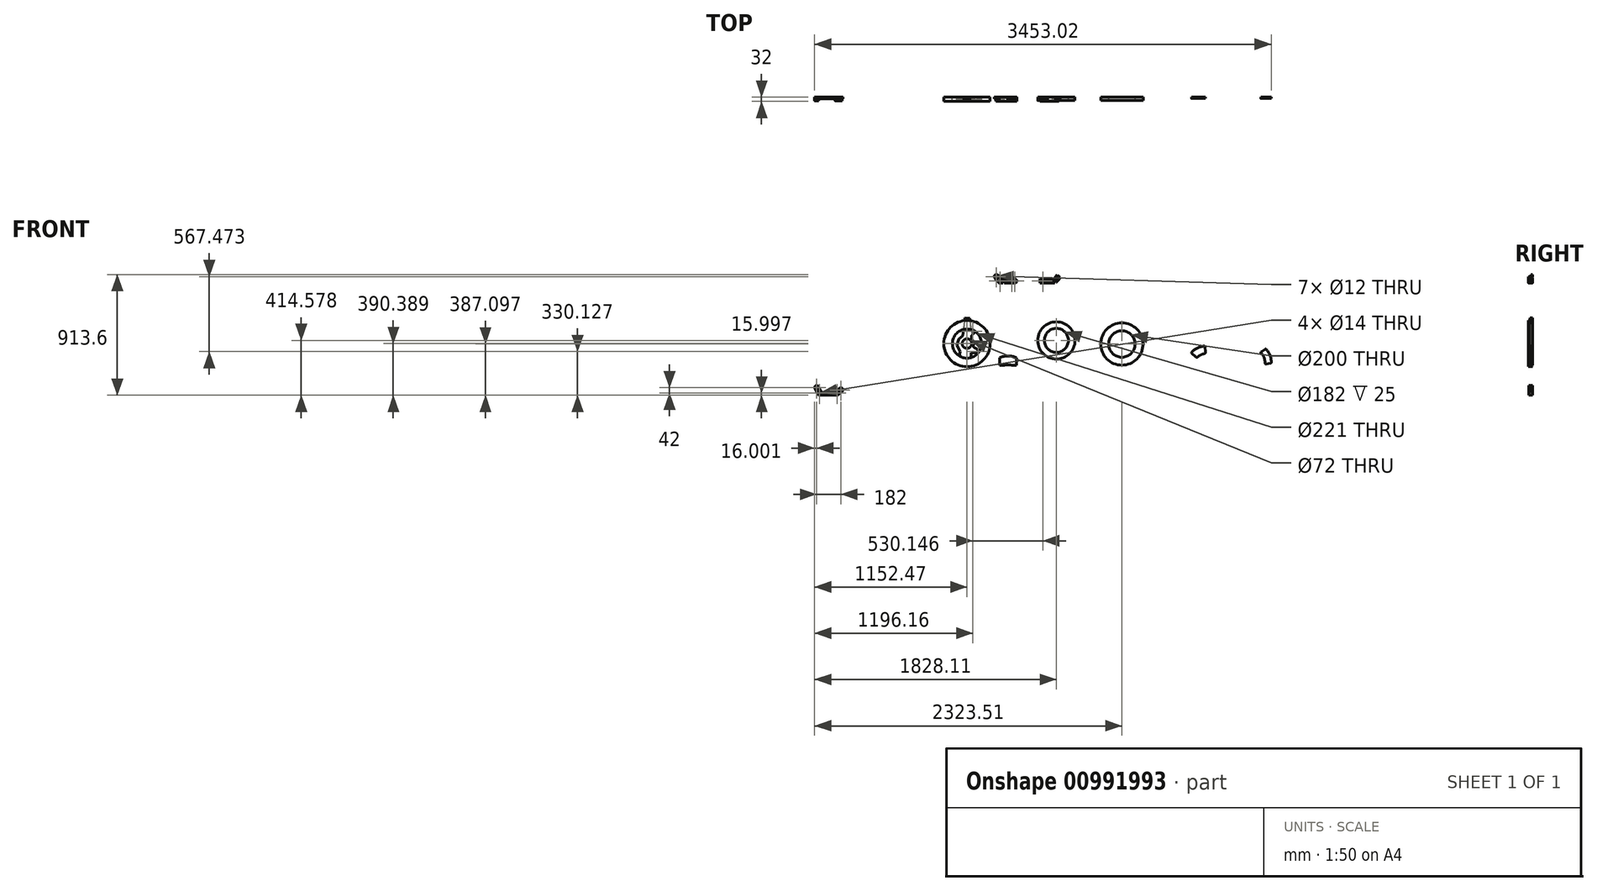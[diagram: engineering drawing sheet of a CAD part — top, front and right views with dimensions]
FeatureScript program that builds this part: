
annotation { "Feature Type Name" : "Feature", "Feature Type Description" : "" }
export const myFeature = defineFeature(function(context is Context, id is Id, definition is map)
    precondition{}
    {
        {
            var Q0;
            Q0=qCreatedBy(makeId("Front.planeOp"),FACE);
            var sketch = newSketch(context, id + "F0", { "sketchPlane" : qUnion([Q0])});
            skLineSegment(sketch, "E0", {"start": v(-162, 0) * mm, "end": v(162, 0) * mm, "construction": true});
            skCircle(sketch, "E1", {"center": v(0, 0) * mm, "radius": 162 * mm});
            skLineSegment(sketch, "E2", {"start": v(0, 162) * mm, "end": v(0, -162) * mm, "construction": true});
            skCircle(sketch, "E3", {"center": v(0, 0) * mm, "radius": 74.5 * mm, "construction": true});
            skLineSegment(sketch, "E4", {"start": v(0, 0) * mm, "end": v(76.6, 64.28) * mm, "construction": true});
            skLineSegment(sketch, "E5", {"start": v(0, 0) * mm, "end": v(77.96, -57.71) * mm, "construction": true});
            skLineSegment(sketch, "E6", {"start": v(76.6, 64.28) * mm, "end": v(77.96, -57.71) * mm, "construction": true});
            skCircle(sketch, "E7", {"center": v(76.6, 64.28) * mm, "radius": 6 * mm});
            skCircle(sketch, "E8", {"center": v(77.96, -57.71) * mm, "radius": 6 * mm});
            skArc(sketch, "E9", {"start": v(88.92, 55.71) * mm, "mid": v(89.19, 72.45) * mm, "end": v(73.8, 79.01) * mm});
            skArc(sketch, "E10", {"start": v(70.62, -70.8) * mm, "mid": v(91.06, -65.02) * mm, "end": v(85.23, -44.6) * mm});
            skLineSegment(sketch, "E11", {"start": v(35.43, -21.17) * mm, "end": v(88.92, 55.71) * mm});
            skLineSegment(sketch, "E12", {"start": v(37.52, -18.16) * mm, "end": v(85.23, -44.6) * mm});
            skArc(sketch, "E13.filletArc", {"start": v(59.66, 13.66) * mm, "mid": v(54.3, -14.26) * mm, "end": v(71.43, -36.95) * mm});
            skLineSegment(sketch, "E14", {"start": v(0, 0) * mm, "end": v(70.26, 84.63) * mm, "construction": true});
            skArc(sketch, "E15", {"start": v(65.94, 99) * mm, "mid": v(56.07, 89.49) * mm, "end": v(58.05, 75.92) * mm});
            skLineSegment(sketch, "E16", {"start": v(70.26, 84.63) * mm, "end": v(102.54, -22.62) * mm, "construction": true});
            skLineSegment(sketch, "E17", {"start": v(102.54, -22.62) * mm, "end": v(0, 0) * mm, "construction": true});
            skCircle(sketch, "E18", {"center": v(70.26, 84.63) * mm, "radius": 6 * mm});
            skCircle(sketch, "E19", {"center": v(102.54, -22.62) * mm, "radius": 6 * mm});
            skLineSegment(sketch, "E20", {"start": v(84.02, 39.53) * mm, "end": v(58.05, 75.92) * mm});
            skLineSegment(sketch, "E21", {"start": v(87.74, -25.06) * mm, "end": v(83.73, -30.58) * mm});
            skArc(sketch, "E22.filletArc", {"start": v(83.73, -30.58) * mm, "mid": v(95.18, 4.43) * mm, "end": v(84.02, 39.53) * mm});
            skArc(sketch, "E23.trimOffspring", {"start": v(87.74, -25.06) * mm, "mid": v(94.6, -35.35) * mm, "end": v(106.86, -36.98) * mm});
            skPoint(sketch, "E24.orphan", {"position": v(76.6, 79.28) * mm});
            skLineSegment(sketch, "E25", {"start": v(8.67, 66.58) * mm, "end": v(73.8, 79.01) * mm});
            skLineSegment(sketch, "E26", {"start": v(77.96, -57.71) * mm, "end": v(102.54, -22.62) * mm});
            skLineSegment(sketch, "E27", {"start": v(360.92, -8.62) * mm, "end": v(248.92, -8.62) * mm, "construction": true});
            skLineSegment(sketch, "E28", {"start": v(248.92, -8.62) * mm, "end": v(222.42, 24.88) * mm, "construction": true});
            skLineSegment(sketch, "E29", {"start": v(222.42, 24.88) * mm, "end": v(386.22, 24.88) * mm, "construction": true});
            skLineSegment(sketch, "E30", {"start": v(222.42, 24.88) * mm, "end": v(222.42, -34.6) * mm, "construction": true});
            skCircle(sketch, "E31", {"center": v(222.42, 24.88) * mm, "radius": 6 * mm});
            skCircle(sketch, "E32", {"center": v(248.92, -8.62) * mm, "radius": 6 * mm});
            skCircle(sketch, "E33", {"center": v(360.92, -8.62) * mm, "radius": 6 * mm});
            skCircle(sketch, "E34", {"center": v(339.42, -8.62) * mm, "radius": 6 * mm});
            skCircle(sketch, "E35", {"center": v(222.42, 24.88) * mm, "radius": 16 * mm});
            skCircle(sketch, "E36", {"center": v(248.92, -8.62) * mm, "radius": 16 * mm});
            skCircle(sketch, "E37", {"center": v(360.92, -8.62) * mm, "radius": 16 * mm});
            skCircle(sketch, "E38", {"center": v(339.42, -8.62) * mm, "radius": 15 * mm});
            skLineSegment(sketch, "E39", {"start": v(248.92, -24.62) * mm, "end": v(360.92, -24.62) * mm});
            skLineSegment(sketch, "E40", {"start": v(360.92, -24.62) * mm, "end": v(360.92, 7.38) * mm});
            skLineSegment(sketch, "E41", {"start": v(360.92, 7.38) * mm, "end": v(266.34, 7.38) * mm});
            skPoint(sketch, "E42.newPointA", {"position": v(248.92, 7.38) * mm});
            skLineSegment(sketch, "E43", {"start": v(37.52, -18.16) * mm, "end": v(77.52, -17.72) * mm});
            skLineSegment(sketch, "E44.trimOffspring", {"start": v(305.92, 7.38) * mm, "end": v(327.67, -17.95) * mm});
            skLineSegment(sketch, "E45", {"start": v(357.92, 7.38) * mm, "end": v(354.13, -11.56) * mm});
            skLineSegment(sketch, "E46.0", {"start": v(236.37, -18.55) * mm, "end": v(209.87, 14.95) * mm});
            skLineSegment(sketch, "E47.0", {"start": v(250.66, 14.97) * mm, "end": v(234.97, 34.8) * mm});
            skLineSegment(sketch, "E48.0", {"start": v(219.55, 2.71) * mm, "end": v(245.14, 21.95) * mm});
            skLineSegment(sketch, "E49", {"start": v(456.63, 91.81) * mm, "end": v(456.63, -58.74) * mm});
            skLineSegment(sketch, "E50.MirrorCS", {"start": v(555.34, 7.38) * mm, "end": v(559.13, -11.56) * mm});
            skLineSegment(sketch, "E51.MirrorCS", {"start": v(664.34, -8.62) * mm, "end": v(690.84, 24.88) * mm, "construction": true});
            skCircle(sketch, "E52.MirrorC", {"center": v(664.34, -8.62) * mm, "radius": 6 * mm});
            skLineSegment(sketch, "E53.MirrorCS", {"start": v(676.89, -18.55) * mm, "end": v(703.39, 14.95) * mm});
            skCircle(sketch, "E54.MirrorC", {"center": v(690.84, 24.88) * mm, "radius": 6 * mm});
            skCircle(sketch, "E55.MirrorC", {"center": v(552.34, -8.62) * mm, "radius": 16 * mm});
            skLineSegment(sketch, "E56.MirrorCS", {"start": v(552.34, 7.38) * mm, "end": v(646.91, 7.38) * mm});
            skCircle(sketch, "E57.MirrorC", {"center": v(664.34, -8.62) * mm, "radius": 16 * mm});
            skLineSegment(sketch, "E58.MirrorCS", {"start": v(607.34, 7.38) * mm, "end": v(585.59, -17.95) * mm});
            skLineSegment(sketch, "E59.MirrorCS", {"start": v(693.7, 2.71) * mm, "end": v(668.12, 21.95) * mm});
            skCircle(sketch, "E60.MirrorC", {"center": v(552.34, -8.62) * mm, "radius": 6 * mm});
            skLineSegment(sketch, "E61.MirrorCS", {"start": v(552.34, -24.62) * mm, "end": v(552.34, 7.38) * mm});
            skLineSegment(sketch, "E62.MirrorCS", {"start": v(552.34, -8.62) * mm, "end": v(664.34, -8.62) * mm, "construction": true});
            skPoint(sketch, "E63.MirrorP", {"position": v(664.34, 7.38) * mm});
            skLineSegment(sketch, "E64.MirrorCS", {"start": v(690.84, 24.88) * mm, "end": v(527.04, 24.88) * mm, "construction": true});
            skLineSegment(sketch, "E65.MirrorCS", {"start": v(690.84, 24.88) * mm, "end": v(690.84, -34.6) * mm, "construction": true});
            skLineSegment(sketch, "E66.MirrorCS", {"start": v(664.34, -24.62) * mm, "end": v(552.34, -24.62) * mm});
            skCircle(sketch, "E67.MirrorC", {"center": v(690.84, 24.88) * mm, "radius": 16 * mm});
            skCircle(sketch, "E68.MirrorC", {"center": v(573.84, -8.62) * mm, "radius": 15 * mm});
            skCircle(sketch, "E69.MirrorC", {"center": v(573.84, -8.62) * mm, "radius": 6 * mm});
            skLineSegment(sketch, "E70.MirrorCS", {"start": v(662.6, 14.97) * mm, "end": v(678.29, 34.8) * mm});
            skPoint(sketch, "E71.visualSharp", {"position": v(256.66, 7.38) * mm});
            skArc(sketch, "E71.filletArc", {"start": v(250.66, 14.97) * mm, "mid": v(257.63, 9.38) * mm, "end": v(266.34, 7.38) * mm});
            skPoint(sketch, "E72.visualSharp", {"position": v(656.6, 7.38) * mm});
            skArc(sketch, "E72.filletArc", {"start": v(646.91, 7.38) * mm, "mid": v(655.63, 9.38) * mm, "end": v(662.6, 14.97) * mm});
            skLineSegment(sketch, "E73", {"start": v(360.92, -14.62) * mm, "end": v(248.92, -14.62) * mm, "construction": true});
            skLineSegment(sketch, "E74", {"start": v(354.92, -8.62) * mm, "end": v(354.92, -24.62) * mm, "construction": true});
            skLineSegment(sketch, "E75.0", {"start": v(338.92, -15.62) * mm, "end": v(338.92, -24.62) * mm, "construction": true});
            skCircle(sketch, "E76", {"center": v(360.92, -8.62) * mm, "radius": 18 * mm, "construction": true});
            skLineSegment(sketch, "E77.0", {"start": v(333.92, -10.62) * mm, "end": v(333.92, -10.62) * mm});
            skLineSegment(sketch, "E78.0", {"start": v(328.92, -15.62) * mm, "end": v(328.92, -24.62) * mm, "construction": true});
            skArc(sketch, "E79.filletArc", {"start": v(333.92, -10.62) * mm, "mid": v(330.38, -12.09) * mm, "end": v(328.92, -15.62) * mm, "construction": true});
            skArc(sketch, "E80.filletArc", {"start": v(338.92, -15.62) * mm, "mid": v(337.45, -12.09) * mm, "end": v(333.92, -10.62) * mm, "construction": true});
            skLineSegment(sketch, "E81.0", {"start": v(280.92, -15.62) * mm, "end": v(280.92, -24.62) * mm});
            skLineSegment(sketch, "E82.0", {"start": v(270.92, -15.62) * mm, "end": v(270.92, -24.62) * mm});
            skArc(sketch, "E83", {"start": v(280.92, -15.62) * mm, "mid": v(275.92, -10.62) * mm, "end": v(270.92, -15.62) * mm});
            skSolve(sketch);
        }
        {
            var Q0;
            Q0=makeQuery(id+"F0.imprint","IMPRINT",FACE,{"disambiguationData":[TD([[makeQuery(id+"F0.imprint","IMPRINT",EDGE,{"derivedFrom":sQuery(id+"F0.wireOp",EDGE,"E31")}),-1.0]])]});
            var Q1;
            {var subQ0=sQuery(id+"F0.wireOp",EDGE,"E47.0");var subQ1=sQuery(id+"F0.wireOp",EDGE,"E35");var subQ2=makeQuery(id+"F0.imprint","INTERSECT",VERTEX,{"derivedFrom":[subQ1,subQ0]});Q1=makeQuery(id+"F0.imprint","IMPRINT",FACE,{"disambiguationData":[TD([[makeQuery(id+"F0.imprint","IMPRINT",EDGE,{"disambiguationData":[TD([[subQ2,1.0]])],"derivedFrom":subQ1}),-1.0]])]});}
            var Q2;
            {var subQ0=sQuery(id+"F0.wireOp",EDGE,"E46.0");var subQ1=sQuery(id+"F0.wireOp",EDGE,"E35");var subQ2=makeQuery(id+"F0.imprint","INTERSECT",VERTEX,{"derivedFrom":[subQ1,subQ0]});Q2=makeQuery(id+"F0.imprint","IMPRINT",FACE,{"disambiguationData":[TD([[makeQuery(id+"F0.imprint","IMPRINT",EDGE,{"disambiguationData":[TD([[subQ2,-1.0]])],"derivedFrom":subQ1}),-1.0]])]});}
            var Q3;
            {var subQ0=sQuery(id+"F0.wireOp",EDGE,"E45");var subQ1=sQuery(id+"F0.wireOp",EDGE,"E37");var subQ2=makeQuery(id+"F0.imprint","INTERSECT",VERTEX,{"derivedFrom":[subQ1,subQ0]});Q3=makeQuery(id+"F0.imprint","IMPRINT",FACE,{"disambiguationData":[TD([[makeQuery(id+"F0.imprint","IMPRINT",EDGE,{"disambiguationData":[TD([[subQ2,-1.0]])],"derivedFrom":subQ1}),1.0]])]});}
            var Q4;
            {var subQ0=sQuery(id+"F0.wireOp",EDGE,"E44.trimOffspring");Q4=makeQuery(id+"F0.imprint","IMPRINT",FACE,{"disambiguationData":[TD([[makeQuery(id+"F0.imprint","IMPRINT",EDGE,{"derivedFrom":subQ0}),1.0]])]});}
            var Q5;
            {var subQ2=sQuery(id+"F0.wireOp",EDGE,"E37");var subQ4=sQuery(id+"F0.wireOp",EDGE,"E34");var subQ6=makeQuery(id+"F0.imprint","INTERSECT",VERTEX,{"disambiguationData":[OD(0.0)],"derivedFrom":[subQ4,subQ2]});Q5=makeQuery(id+"F0.imprint","IMPRINT",FACE,{"disambiguationData":[TD([[makeQuery(id+"F0.imprint","IMPRINT",EDGE,{"disambiguationData":[TD([[subQ6,1.0]])],"derivedFrom":subQ4}),-1.0]])]});}
            var Q6;
            {var subQ0=sQuery(id+"F0.wireOp",EDGE,"E37");var subQ1=sQuery(id+"F0.wireOp",EDGE,"E34");var subQ7=makeQuery(id+"F0.imprint","INTERSECT",VERTEX,{"disambiguationData":[OD(0.0)],"derivedFrom":[subQ1,subQ0]});Q6=makeQuery(id+"F0.imprint","IMPRINT",FACE,{"disambiguationData":[TD([[makeQuery(id+"F0.imprint","IMPRINT",EDGE,{"disambiguationData":[TD([[subQ7,-1.0]])],"derivedFrom":subQ1}),-1.0]])]});}
            extrude(context, id + "F1", {"entities" : qUnion([Q0, Q1, Q2, Q3, Q4, Q5, Q6]), "depth" : 12 * mm, "offsetDistance" : 25 * mm});
        }
        {
            var Q0;
            {var subQ0=sQuery(id+"F0.wireOp",EDGE,"E40");var subQ1=sQuery(id+"F0.wireOp",EDGE,"E33");var subQ2=makeQuery(id+"F0.imprint","INTERSECT",VERTEX,{"disambiguationData":[OD(0.0)],"derivedFrom":[subQ1,subQ0]});Q0=makeQuery(id+"F0.imprint","IMPRINT",FACE,{"disambiguationData":[TD([[makeQuery(id+"F0.imprint","IMPRINT",EDGE,{"disambiguationData":[TD([[subQ2,-1.0]])],"derivedFrom":subQ1}),-1.0]])]});}
            var Q1;
            {var subQ5=sQuery(id+"F0.wireOp",EDGE,"E40");var subQ9=sQuery(id+"F0.wireOp",EDGE,"E33");var subQ10=makeQuery(id+"F0.imprint","INTERSECT",VERTEX,{"disambiguationData":[OD(0.0)],"derivedFrom":[subQ9,subQ5]});Q1=makeQuery(id+"F0.imprint","IMPRINT",FACE,{"disambiguationData":[TD([[makeQuery(id+"F0.imprint","IMPRINT",EDGE,{"disambiguationData":[TD([[subQ10,1.0]])],"derivedFrom":subQ9}),-1.0]])]});}
            var Q2;
            {var subQ0=sQuery(id+"F0.wireOp",EDGE,"E41");var subQ3=sQuery(id+"F0.wireOp",EDGE,"E45");var subQ5=makeQuery(id+"F0.imprint","INTERSECT",VERTEX,{"derivedFrom":[subQ0,subQ3]});Q2=makeQuery(id+"F0.imprint","IMPRINT",FACE,{"disambiguationData":[TD([[makeQuery(id+"F0.imprint","IMPRINT",EDGE,{"disambiguationData":[TD([[subQ5,-1.0]])],"derivedFrom":subQ3}),1.0]])]});}
            var Q3;
            {var subQ12=sQuery(id+"F0.wireOp",EDGE,"E39");Q3=makeQuery(id+"F0.imprint","IMPRINT",FACE,{"disambiguationData":[TD([[makeQuery(id+"F0.imprint","IMPRINT",EDGE,{"derivedFrom":subQ12}),1.0]])]});}
            var Q4;
            Q4=makeQuery(id+"F0.imprint","IMPRINT",FACE,{"disambiguationData":[TD([[makeQuery(id+"F0.imprint","IMPRINT",EDGE,{"derivedFrom":sQuery(id+"F0.wireOp",EDGE,"E32")}),-1.0]])]});
            extrude(context, id + "F2", {"entities" : qUnion([Q0, Q1, Q2, Q3, Q4]), "depth" : 30 * mm, "offsetDistance" : 25 * mm});
        }
        {
            var Q0;
            {var subQ0=sQuery(id+"F0.wireOp",EDGE,"E58.MirrorCS");Q0=makeQuery(id+"F0.imprint","IMPRINT",FACE,{"disambiguationData":[TD([[makeQuery(id+"F0.imprint","IMPRINT",EDGE,{"derivedFrom":subQ0}),-1.0]])]});}
            var Q1;
            {var subQ0=sQuery(id+"F0.wireOp",EDGE,"E68.MirrorC");var subQ2=sQuery(id+"F0.wireOp",EDGE,"E55.MirrorC");var subQ3=makeQuery(id+"F0.imprint","INTERSECT",VERTEX,{"disambiguationData":[OD(0.0)],"derivedFrom":[subQ2,subQ0]});Q1=makeQuery(id+"F0.imprint","IMPRINT",FACE,{"disambiguationData":[TD([[makeQuery(id+"F0.imprint","IMPRINT",EDGE,{"disambiguationData":[TD([[subQ3,-1.0]])],"derivedFrom":subQ2}),1.0]])]});}
            var Q2;
            {var subQ0=sQuery(id+"F0.wireOp",EDGE,"E68.MirrorC");var subQ2=sQuery(id+"F0.wireOp",EDGE,"E55.MirrorC");var subQ4=makeQuery(id+"F0.imprint","INTERSECT",VERTEX,{"disambiguationData":[OD(0.0)],"derivedFrom":[subQ2,subQ0]});Q2=makeQuery(id+"F0.imprint","IMPRINT",FACE,{"disambiguationData":[TD([[makeQuery(id+"F0.imprint","IMPRINT",EDGE,{"disambiguationData":[TD([[subQ4,-1.0]])],"derivedFrom":subQ2}),-1.0]])]});}
            var Q3;
            {var subQ0=sQuery(id+"F0.wireOp",EDGE,"E68.MirrorC");var subQ1=sQuery(id+"F0.wireOp",EDGE,"E50.MirrorCS");var subQ2=makeQuery(id+"F0.imprint","INTERSECT",VERTEX,{"derivedFrom":[subQ1,subQ0]});Q3=makeQuery(id+"F0.imprint","IMPRINT",FACE,{"disambiguationData":[TD([[makeQuery(id+"F0.imprint","IMPRINT",EDGE,{"disambiguationData":[TD([[subQ2,1.0]])],"derivedFrom":subQ1}),1.0]])]});}
            var Q4;
            Q4=makeQuery(id+"F0.imprint","IMPRINT",FACE,{"disambiguationData":[TD([[makeQuery(id+"F0.imprint","IMPRINT",EDGE,{"derivedFrom":sQuery(id+"F0.wireOp",EDGE,"E54.MirrorC")}),1.0]])]});
            var Q5;
            {var subQ0=sQuery(id+"F0.wireOp",EDGE,"E70.MirrorCS");var subQ1=sQuery(id+"F0.wireOp",EDGE,"E59.MirrorCS");var subQ2=makeQuery(id+"F0.imprint","INTERSECT",VERTEX,{"derivedFrom":[subQ1,subQ0]});Q5=makeQuery(id+"F0.imprint","IMPRINT",FACE,{"disambiguationData":[TD([[makeQuery(id+"F0.imprint","IMPRINT",EDGE,{"disambiguationData":[TD([[subQ2,1.0]])],"derivedFrom":subQ1}),-1.0]])]});}
            var Q6;
            {var subQ0=sQuery(id+"F0.wireOp",EDGE,"E67.MirrorC");var subQ1=sQuery(id+"F0.wireOp",EDGE,"E53.MirrorCS");var subQ2=makeQuery(id+"F0.imprint","INTERSECT",VERTEX,{"derivedFrom":[subQ1,subQ0]});Q6=makeQuery(id+"F0.imprint","IMPRINT",FACE,{"disambiguationData":[TD([[makeQuery(id+"F0.imprint","IMPRINT",EDGE,{"disambiguationData":[TD([[subQ2,1.0]])],"derivedFrom":subQ1}),1.0]])]});}
            extrude(context, id + "F3", {"entities" : qUnion([Q0, Q1, Q2, Q3, Q4, Q5, Q6]), "depth" : 12 * mm, "offsetDistance" : 25 * mm});
        }
        {
            var Q0;
            {var subQ0=sQuery(id+"F0.wireOp",EDGE,"E61.MirrorCS");var subQ4=sQuery(id+"F0.wireOp",EDGE,"E60.MirrorC");var subQ5=makeQuery(id+"F0.imprint","INTERSECT",VERTEX,{"disambiguationData":[OD(0.0)],"derivedFrom":[subQ4,subQ0]});Q0=makeQuery(id+"F0.imprint","IMPRINT",FACE,{"disambiguationData":[TD([[makeQuery(id+"F0.imprint","IMPRINT",EDGE,{"disambiguationData":[TD([[subQ5,-1.0]])],"derivedFrom":subQ4}),1.0]])]});}
            var Q1;
            {var subQ6=sQuery(id+"F0.wireOp",EDGE,"E68.MirrorC");var subQ9=sQuery(id+"F0.wireOp",EDGE,"E50.MirrorCS");var subQ11=makeQuery(id+"F0.imprint","INTERSECT",VERTEX,{"derivedFrom":[subQ9,subQ6]});Q1=makeQuery(id+"F0.imprint","IMPRINT",FACE,{"disambiguationData":[TD([[makeQuery(id+"F0.imprint","IMPRINT",EDGE,{"disambiguationData":[TD([[subQ11,1.0]])],"derivedFrom":subQ9}),-1.0]])]});}
            var Q2;
            {var subQ0=sQuery(id+"F0.wireOp",EDGE,"E56.MirrorCS");var subQ1=sQuery(id+"F0.wireOp",EDGE,"E50.MirrorCS");var subQ2=makeQuery(id+"F0.imprint","INTERSECT",VERTEX,{"derivedFrom":[subQ1,subQ0]});Q2=makeQuery(id+"F0.imprint","IMPRINT",FACE,{"disambiguationData":[TD([[makeQuery(id+"F0.imprint","IMPRINT",EDGE,{"disambiguationData":[TD([[subQ2,-1.0]])],"derivedFrom":subQ1}),-1.0]])]});}
            var Q3;
            {var subQ9=sQuery(id+"F0.wireOp",EDGE,"E58.MirrorCS");Q3=makeQuery(id+"F0.imprint","IMPRINT",FACE,{"disambiguationData":[TD([[makeQuery(id+"F0.imprint","IMPRINT",EDGE,{"derivedFrom":subQ9}),1.0]])]});}
            var Q4;
            Q4=makeQuery(id+"F0.imprint","IMPRINT",FACE,{"disambiguationData":[TD([[makeQuery(id+"F0.imprint","IMPRINT",EDGE,{"derivedFrom":sQuery(id+"F0.wireOp",EDGE,"E52.MirrorC")}),1.0]])]});
            extrude(context, id + "F4", {"entities" : qUnion([Q0, Q1, Q2, Q3, Q4]), "depth" : 30 * mm, "offsetDistance" : 25 * mm});
        }
        {
            var Q0;
            Q0=qCreatedBy(makeId("Front.planeOp"),FACE);
            var sketch = newSketch(context, id + "F5", { "sketchPlane" : qUnion([Q0])});
            skLineSegment(sketch, "E84", {"start": v(0, -307.33) * mm, "end": v(0, -657.33) * mm, "construction": true});
            skLineSegment(sketch, "E85", {"start": v(-175, -482.33) * mm, "end": v(175, -482.33) * mm, "construction": true});
            skCircle(sketch, "E86", {"center": v(0, -482.33) * mm, "radius": 36 * mm});
            skCircle(sketch, "E87", {"center": v(0, -482.33) * mm, "radius": 57.15 * mm, "construction": true});
            skCircle(sketch, "E88", {"center": v(0, -482.33) * mm, "radius": 175 * mm});
            skCircle(sketch, "E89", {"center": v(57.15, -482.33) * mm, "radius": 6.1 * mm});
            skCircle(sketch, "E90.1.0", {"center": v(17.66, -536.68) * mm, "radius": 6.1 * mm});
            skCircle(sketch, "E90.2.0", {"center": v(-46.24, -515.92) * mm, "radius": 6.1 * mm});
            skCircle(sketch, "E90.3.0", {"center": v(-46.24, -448.74) * mm, "radius": 6.1 * mm});
            skCircle(sketch, "E90.4.0", {"center": v(17.66, -427.98) * mm, "radius": 6.1 * mm});
            skCircle(sketch, "E91", {"center": v(43.7, -387.95) * mm, "radius": 6 * mm});
            skCircle(sketch, "E92", {"center": v(84.76, -542.6) * mm, "radius": 6 * mm});
            skArc(sketch, "E93", {"start": v(48.18, -495.7) * mm, "mid": v(48.92, -471.99) * mm, "end": v(38.64, -450.6) * mm});
            skArc(sketch, "E94", {"start": v(84.07, -554.44) * mm, "mid": v(96.16, -545.89) * mm, "end": v(90.49, -532.2) * mm});
            skArc(sketch, "E95", {"start": v(54.93, -397.9) * mm, "mid": v(57.08, -381.18) * mm, "end": v(42.33, -373.02) * mm});
            skLineSegment(sketch, "E96", {"start": v(55.4, -512.86) * mm, "end": v(90.49, -532.2) * mm});
            skArc(sketch, "E97.filletArc", {"start": v(48.18, -495.7) * mm, "mid": v(48.8, -505.54) * mm, "end": v(55.4, -512.86) * mm});
            skLineSegment(sketch, "E98", {"start": v(39.29, -415.57) * mm, "end": v(54.93, -397.9) * mm});
            skPoint(sketch, "E99.visualSharp", {"position": v(20.54, -436.75) * mm});
            skArc(sketch, "E99.filletArc", {"start": v(39.29, -415.57) * mm, "mid": v(32.5, -432.96) * mm, "end": v(38.64, -450.6) * mm});
            skLineSegment(sketch, "E100", {"start": v(21.57, -550.77) * mm, "end": v(84.07, -554.44) * mm});
            skLineSegment(sketch, "E101", {"start": v(10.62, -375.9) * mm, "end": v(42.33, -373.02) * mm});
            skCircle(sketch, "E102", {"center": v(0, -482.33) * mm, "radius": 110.5 * mm});
            skLineSegment(sketch, "E103.0", {"start": v(246.52, -647.5) * mm, "end": v(277.02, -647.5) * mm});
            skLineSegment(sketch, "E104", {"start": v(246.52, -647.5) * mm, "end": v(246.52, -588.5) * mm});
            skLineSegment(sketch, "E105.0", {"start": v(374.52, -647.5) * mm, "end": v(374.52, -588.5) * mm});
            skArc(sketch, "E106", {"start": v(374.52, -588.5) * mm, "mid": v(310.52, -576.5) * mm, "end": v(246.52, -588.5) * mm});
            skArc(sketch, "E107", {"start": v(344.02, -647.5) * mm, "mid": v(310.52, -642.32) * mm, "end": v(277.02, -647.5) * mm});
            skLineSegment(sketch, "E108.trimOffspring", {"start": v(344.02, -647.5) * mm, "end": v(374.52, -647.5) * mm});
            skLineSegment(sketch, "E109", {"start": v(20.52, -289.6) * mm, "end": v(27.5, -374.37) * mm});
            skLineSegment(sketch, "E110", {"start": v(-17.97, -286.17) * mm, "end": v(-32.55, -424.34) * mm});
            skLineSegment(sketch, "E111", {"start": v(-32.55, -424.34) * mm, "end": v(-59.93, -445.81) * mm});
            skLineSegment(sketch, "E112", {"start": v(-59.93, -445.81) * mm, "end": v(-76.28, -493.3) * mm});
            skLineSegment(sketch, "E113", {"start": v(-76.28, -493.3) * mm, "end": v(-52.2, -540.3) * mm});
            skLineSegment(sketch, "E114", {"start": v(-52.2, -540.3) * mm, "end": v(-58.88, -590.81) * mm});
            skLineSegment(sketch, "E115", {"start": v(-58.88, -590.81) * mm, "end": v(28.35, -593.9) * mm});
            skLineSegment(sketch, "E116", {"start": v(20.52, -289.6) * mm, "end": v(-17.97, -286.17) * mm});
            skCircle(sketch, "E117", {"center": v(0, -482.33) * mm, "radius": 104 * mm, "construction": true});
            skCircle(sketch, "E118", {"center": v(75.37, -545.98) * mm, "radius": 7 * mm, "construction": true});
            skCircle(sketch, "E119", {"center": v(36.66, -390.74) * mm, "radius": 7 * mm, "construction": true});
            skCircle(sketch, "E120", {"center": v(0, -482.33) * mm, "radius": 98.65 * mm, "construction": true});
            skArc(sketch, "E121", {"start": v(39.16, -556.6) * mm, "mid": v(87.53, -496.9) * mm, "end": v(60.86, -424.84) * mm, "construction": true});
            skLineSegment(sketch, "E122.0", {"start": v(30.14, -551.27) * mm, "end": v(30.14, -603.24) * mm});
            skCircle(sketch, "E123", {"center": v(43.08, -571.08) * mm, "radius": 7 * mm, "construction": true});
            skCircle(sketch, "E124", {"center": v(70.65, -413.47) * mm, "radius": 7 * mm, "construction": true});
            skLineSegment(sketch, "E125", {"start": v(70.65, -413.47) * mm, "end": v(43.08, -571.08) * mm, "construction": true});
            skCircle(sketch, "E126", {"center": v(70.65, -413.47) * mm, "radius": 15 * mm, "construction": true});
            skCircle(sketch, "E127", {"center": v(43.08, -571.08) * mm, "radius": 15 * mm, "construction": true});
            skLineSegment(sketch, "E128", {"start": v(56.87, -492.28) * mm, "end": v(87.4, -497.62) * mm, "construction": true});
            skArc(sketch, "E129.0", {"start": v(100.46, -540.33) * mm, "mid": v(114.99, -502.42) * mm, "end": v(114.14, -461.83) * mm, "construction": true});
            skLineSegment(sketch, "E130", {"start": v(43.08, -571.08) * mm, "end": v(100.46, -540.33) * mm, "construction": true});
            skLineSegment(sketch, "E131", {"start": v(70.65, -413.47) * mm, "end": v(114.14, -461.83) * mm, "construction": true});
            skLineSegment(sketch, "E132", {"start": v(-554.05, -351.94) * mm, "end": v(-554.05, -701.94) * mm, "construction": true});
            skLineSegment(sketch, "E133", {"start": v(-729.05, -526.94) * mm, "end": v(-379.05, -526.94) * mm, "construction": true});
            skCircle(sketch, "E134", {"center": v(-554.05, -526.94) * mm, "radius": 36 * mm});
            skCircle(sketch, "E135", {"center": v(-510.35, -432.56) * mm, "radius": 6 * mm});
            skCircle(sketch, "E136", {"center": v(-471.16, -589.74) * mm, "radius": 6 * mm});
            skArc(sketch, "E137", {"start": v(-505.87, -540.31) * mm, "mid": v(-505.13, -516.6) * mm, "end": v(-515.4, -495.2) * mm, "construction": true});
            skArc(sketch, "E138", {"start": v(-472.03, -604.72) * mm, "mid": v(-456.74, -593.9) * mm, "end": v(-463.92, -576.6) * mm, "construction": true});
            skArc(sketch, "E139", {"start": v(-499.12, -442.5) * mm, "mid": v(-496.97, -425.78) * mm, "end": v(-511.72, -417.62) * mm, "construction": true});
            skLineSegment(sketch, "E140", {"start": v(-498.66, -557.46) * mm, "end": v(-463.92, -576.6) * mm, "construction": true});
            skArc(sketch, "E141.filletArc", {"start": v(-505.87, -540.31) * mm, "mid": v(-505.24, -550.14) * mm, "end": v(-498.66, -557.46) * mm, "construction": true});
            skLineSegment(sketch, "E142", {"start": v(-514.76, -460.17) * mm, "end": v(-499.12, -442.5) * mm, "construction": true});
            skArc(sketch, "E143.filletArc", {"start": v(-514.76, -460.17) * mm, "mid": v(-521.54, -477.57) * mm, "end": v(-515.4, -495.2) * mm, "construction": true});
            skLineSegment(sketch, "E144", {"start": v(-518.55, -601.99) * mm, "end": v(-472.03, -604.72) * mm, "construction": true});
            skLineSegment(sketch, "E145", {"start": v(-543.42, -420.5) * mm, "end": v(-511.72, -417.62) * mm, "construction": true});
            skLineSegment(sketch, "E146", {"start": v(-533.53, -334.21) * mm, "end": v(-526.55, -418.97) * mm, "construction": true});
            skArc(sketch, "E147", {"start": v(-514.9, -601.2) * mm, "mid": v(-466.52, -541.5) * mm, "end": v(-493.19, -469.44) * mm, "construction": true});
            skLineSegment(sketch, "E148.0", {"start": v(-525.96, -608.97) * mm, "end": v(-525.96, -653.52) * mm, "construction": true});
            skCircle(sketch, "E149", {"center": v(-510.96, -615.69) * mm, "radius": 7 * mm});
            skCircle(sketch, "E150", {"center": v(-483.4, -458.08) * mm, "radius": 7 * mm});
            skCircle(sketch, "E151", {"center": v(-483.4, -458.08) * mm, "radius": 15 * mm, "construction": true});
            skCircle(sketch, "E152", {"center": v(-510.96, -615.69) * mm, "radius": 15 * mm, "construction": true});
            skPoint(sketch, "E153.visualSharp", {"position": v(-525.96, -601.55) * mm});
            skArc(sketch, "E153.filletArc", {"start": v(-518.55, -601.99) * mm, "mid": v(-523.77, -603.88) * mm, "end": v(-525.96, -608.97) * mm, "construction": true});
            skCircle(sketch, "E154", {"center": v(-510.35, -432.56) * mm, "radius": 16 * mm});
            skCircle(sketch, "E155", {"center": v(-483.4, -458.08) * mm, "radius": 16 * mm});
            skCircle(sketch, "E156", {"center": v(-471.16, -589.74) * mm, "radius": 16 * mm});
            skArc(sketch, "E157", {"start": v(-524.96, -623.43) * mm, "mid": v(-494.96, -615.69) * mm, "end": v(-524.96, -607.94) * mm});
            skLineSegment(sketch, "E158", {"start": v(-479.76, -497.23) * mm, "end": v(-475.06, -547.7) * mm});
            skLineSegment(sketch, "E159", {"start": v(-510.96, -615.69) * mm, "end": v(-471.16, -589.74) * mm});
            skLineSegment(sketch, "E160", {"start": v(-483.4, -458.08) * mm, "end": v(-510.35, -432.56) * mm});
            skLineSegment(sketch, "E161.0", {"start": v(-472.4, -446.46) * mm, "end": v(-499.36, -420.94) * mm});
            skLineSegment(sketch, "E162.0", {"start": v(-492.09, -471.88) * mm, "end": v(-521.35, -444.18) * mm});
            skLineSegment(sketch, "E163.0", {"start": v(-467.47, -456.6) * mm, "end": v(-455.22, -588.26) * mm});
            skLineSegment(sketch, "E164.0", {"start": v(-502.23, -629.1) * mm, "end": v(-462.42, -603.15) * mm});
            skLineSegment(sketch, "E165.0", {"start": v(-519.7, -602.28) * mm, "end": v(-493.05, -584.92) * mm});
            skLineSegment(sketch, "E166", {"start": v(-498.74, -443.56) * mm, "end": v(-509.34, -455.55) * mm});
            skLineSegment(sketch, "E167", {"start": v(-493.9, -470.18) * mm, "end": v(-547.62, -526.94) * mm});
            skArc(sketch, "E168.filletArc", {"start": v(-479.76, -497.23) * mm, "mid": v(-483.62, -483.43) * mm, "end": v(-492.09, -471.88) * mm});
            skArc(sketch, "E169.filletArc", {"start": v(-493.05, -584.92) * mm, "mid": v(-478.88, -568.81) * mm, "end": v(-475.06, -547.7) * mm});
            skLineSegment(sketch, "E170.0", {"start": v(-520.54, -602.87) * mm, "end": v(-466.83, -606.03) * mm});
            skLineSegment(sketch, "E171.0", {"start": v(-524.96, -607.94) * mm, "end": v(-524.96, -653.52) * mm});
            skLineSegment(sketch, "E172", {"start": v(-1114.47, -872.72) * mm, "end": v(-828.83, -872.72) * mm});
            skLineSegment(sketch, "E173.0", {"start": v(-1072.2, -856.72) * mm, "end": v(-1021.52, -856.72) * mm});
            skLineSegment(sketch, "E174", {"start": v(-471.16, -589.74) * mm, "end": v(-455.22, -588.26) * mm});
            skLineSegment(sketch, "E175", {"start": v(-1114.47, -872.72) * mm, "end": v(-1114.47, -771.24) * mm, "construction": true});
            skLineSegment(sketch, "E176.0", {"start": v(-1136.47, -872.72) * mm, "end": v(-1136.47, -771.24) * mm, "construction": true});
            skLineSegment(sketch, "E177.0", {"start": v(-982.22, -872.72) * mm, "end": v(-982.22, -771.24) * mm, "construction": true});
            skLineSegment(sketch, "E178.0", {"start": v(-954.47, -872.72) * mm, "end": v(-954.47, -771.24) * mm, "construction": true});
            skLineSegment(sketch, "E179.0", {"start": v(-982.22, -832.22) * mm, "end": v(-828.83, -832.22) * mm, "construction": true});
            skLineSegment(sketch, "E180.0", {"start": v(-1136.47, -814.72) * mm, "end": v(-1114.47, -814.72) * mm, "construction": true});
            skCircle(sketch, "E181", {"center": v(-1136.47, -814.72) * mm, "radius": 7 * mm});
            skCircle(sketch, "E182", {"center": v(-1114.47, -856.72) * mm, "radius": 7 * mm});
            skCircle(sketch, "E183", {"center": v(-982.22, -856.72) * mm, "radius": 7 * mm});
            skCircle(sketch, "E184", {"center": v(-954.47, -832.22) * mm, "radius": 7 * mm});
            skArc(sketch, "E185", {"start": v(-1130.24, -854.04) * mm, "mid": v(-1126.7, -867.05) * mm, "end": v(-1114.47, -872.72) * mm});
            skArc(sketch, "E186", {"start": v(-992.8, -844.73) * mm, "mid": v(-994.21, -867.31) * mm, "end": v(-971.63, -868.72) * mm});
            skArc(sketch, "E187", {"start": v(-966.46, -842.81) * mm, "mid": v(-938.5, -833.22) * mm, "end": v(-965.06, -820.23) * mm});
            skArc(sketch, "E188", {"start": v(-1122.3, -807.3) * mm, "mid": v(-1124.4, -804.23) * mm, "end": v(-1127.14, -801.72) * mm});
            skLineSegment(sketch, "E189", {"start": v(-1114.47, -856.72) * mm, "end": v(-1136.47, -814.72) * mm, "construction": true});
            skLineSegment(sketch, "E190", {"start": v(-982.22, -856.72) * mm, "end": v(-954.47, -832.22) * mm, "construction": true});
            skLineSegment(sketch, "E191.0", {"start": v(-1128.64, -864.15) * mm, "end": v(-1150.64, -822.15) * mm});
            skLineSegment(sketch, "E192.0", {"start": v(-971.63, -868.72) * mm, "end": v(-943.88, -844.22) * mm});
            skLineSegment(sketch, "E193.0", {"start": v(-995.05, -846.7) * mm, "end": v(-965.06, -820.23) * mm});
            skLineSegment(sketch, "E194.0", {"start": v(-1107.64, -835.28) * mm, "end": v(-1122.3, -807.3) * mm});
            skArc(sketch, "E195.filletArc", {"start": v(-1021.52, -856.72) * mm, "mid": v(-1007.37, -854.14) * mm, "end": v(-995.05, -846.7) * mm});
            skArc(sketch, "E196.filletArc", {"start": v(-1107.64, -835.28) * mm, "mid": v(-1092.91, -850.95) * mm, "end": v(-1072.2, -856.72) * mm});
            skLineSegment(sketch, "E197", {"start": v(-966.46, -842.81) * mm, "end": v(-977.05, -830.82) * mm});
            skLineSegment(sketch, "E198", {"start": v(-1122.3, -807.3) * mm, "end": v(-1130.24, -854.04) * mm});
            skLineSegment(sketch, "E199", {"start": v(-1127.14, -801.72) * mm, "end": v(-1142.04, -799.72) * mm});
            skArc(sketch, "E200.trimOffspring", {"start": v(-1142.04, -799.72) * mm, "mid": v(-1151.4, -809) * mm, "end": v(-1150.64, -822.15) * mm});
            skLineSegment(sketch, "E201", {"start": v(-1206.67, -1219.87) * mm, "end": v(-921.03, -1219.87) * mm});
            skLineSegment(sketch, "E202.0", {"start": v(-1164.4, -1203.87) * mm, "end": v(-1113.73, -1203.87) * mm});
            skLineSegment(sketch, "E203", {"start": v(-1206.67, -1219.87) * mm, "end": v(-1206.67, -1118.39) * mm, "construction": true});
            skLineSegment(sketch, "E204.0", {"start": v(-1228.67, -1219.87) * mm, "end": v(-1228.67, -1118.39) * mm, "construction": true});
            skLineSegment(sketch, "E205.0", {"start": v(-1074.42, -1219.87) * mm, "end": v(-1074.42, -1118.39) * mm, "construction": true});
            skLineSegment(sketch, "E206.0", {"start": v(-1046.67, -1219.87) * mm, "end": v(-1046.67, -1118.39) * mm, "construction": true});
            skLineSegment(sketch, "E207.0", {"start": v(-1074.42, -1179.37) * mm, "end": v(-921.03, -1179.37) * mm, "construction": true});
            skLineSegment(sketch, "E208.0", {"start": v(-1228.67, -1161.87) * mm, "end": v(-1206.67, -1161.87) * mm, "construction": true});
            skCircle(sketch, "E209", {"center": v(-1228.67, -1161.87) * mm, "radius": 7 * mm});
            skCircle(sketch, "E210", {"center": v(-1206.67, -1203.87) * mm, "radius": 7 * mm});
            skCircle(sketch, "E211", {"center": v(-1074.42, -1203.87) * mm, "radius": 7 * mm});
            skCircle(sketch, "E212", {"center": v(-1046.67, -1179.37) * mm, "radius": 7 * mm});
            skArc(sketch, "E213", {"start": v(-1222.44, -1201.19) * mm, "mid": v(-1218.9, -1214.2) * mm, "end": v(-1206.67, -1219.87) * mm});
            skArc(sketch, "E214", {"start": v(-1085, -1191.88) * mm, "mid": v(-1086.41, -1214.46) * mm, "end": v(-1063.83, -1215.86) * mm});
            skArc(sketch, "E215", {"start": v(-1058.66, -1189.96) * mm, "mid": v(-1030.7, -1180.36) * mm, "end": v(-1057.26, -1167.38) * mm});
            skArc(sketch, "E216", {"start": v(-1214.5, -1154.45) * mm, "mid": v(-1216.6, -1151.37) * mm, "end": v(-1219.34, -1148.87) * mm});
            skLineSegment(sketch, "E217", {"start": v(-1206.67, -1203.87) * mm, "end": v(-1228.67, -1161.87) * mm, "construction": true});
            skLineSegment(sketch, "E218", {"start": v(-1074.42, -1203.87) * mm, "end": v(-1046.67, -1179.37) * mm, "construction": true});
            skLineSegment(sketch, "E219.0", {"start": v(-1220.84, -1211.3) * mm, "end": v(-1242.84, -1169.3) * mm});
            skLineSegment(sketch, "E220.0", {"start": v(-1063.83, -1215.86) * mm, "end": v(-1036.08, -1191.36) * mm});
            skLineSegment(sketch, "E221.0", {"start": v(-1087.25, -1193.86) * mm, "end": v(-1057.26, -1167.38) * mm});
            skLineSegment(sketch, "E222.0", {"start": v(-1199.84, -1182.43) * mm, "end": v(-1214.5, -1154.45) * mm});
            skArc(sketch, "E223.filletArc", {"start": v(-1113.73, -1203.87) * mm, "mid": v(-1099.57, -1201.28) * mm, "end": v(-1087.25, -1193.86) * mm});
            skArc(sketch, "E224.filletArc", {"start": v(-1199.84, -1182.43) * mm, "mid": v(-1185.11, -1198.1) * mm, "end": v(-1164.4, -1203.87) * mm});
            skLineSegment(sketch, "E225", {"start": v(-1058.66, -1189.96) * mm, "end": v(-1069.25, -1177.96) * mm});
            skLineSegment(sketch, "E226", {"start": v(-1214.5, -1154.45) * mm, "end": v(-1222.44, -1201.19) * mm});
            skLineSegment(sketch, "E227", {"start": v(-1219.34, -1148.87) * mm, "end": v(-1234.24, -1146.87) * mm});
            skArc(sketch, "E228.trimOffspring", {"start": v(-1234.24, -1146.87) * mm, "mid": v(-1243.6, -1156.14) * mm, "end": v(-1242.84, -1169.3) * mm});
            skCircle(sketch, "E229", {"center": v(-1206.67, -1203.87) * mm, "radius": 160 * mm});
            skCircle(sketch, "E230", {"center": v(-1228.67, -1161.87) * mm, "radius": 159 * mm});
            skLineSegment(sketch, "E231", {"start": v(-1206.67, -1203.87) * mm, "end": v(-1046.67, -1179.37) * mm});
            skLineSegment(sketch, "E232", {"start": v(-1228.67, -1161.87) * mm, "end": v(-1074.42, -1203.87) * mm});
            skSolve(sketch);
        }
        {
            var Q0;
            Q0=makeQuery(id+"F5.imprint","IMPRINT",FACE,{"disambiguationData":[TD([[makeQuery(id+"F5.imprint","IMPRINT",EDGE,{"derivedFrom":sQuery(id+"F5.wireOp",EDGE,"E103.0")}),1.0]])]});
            extrude(context, id + "F6", {"entities" : qUnion([Q0]), "depth" : 10 * mm, "offsetDistance" : 25 * mm});
        }
        {
            var Q0;
            Q0=makeQuery(id+"F5.imprint","IMPRINT",FACE,{"disambiguationData":[TD([[makeQuery(id+"F5.imprint","IMPRINT",EDGE,{"derivedFrom":sQuery(id+"F5.wireOp",EDGE,"E88")}),1.0]])]});
            var Q1;
            {var subQ0=sQuery(id+"F5.wireOp",EDGE,"E101");var subQ1=sQuery(id+"F5.wireOp",EDGE,"E95");var subQ2=makeQuery(id+"F5.imprint","INTERSECT",VERTEX,{"derivedFrom":[subQ1,subQ0]});Q1=makeQuery(id+"F5.imprint","IMPRINT",FACE,{"disambiguationData":[TD([[makeQuery(id+"F5.imprint","IMPRINT",EDGE,{"disambiguationData":[TD([[subQ2,1.0]])],"derivedFrom":subQ1}),1.0]])]});}
            var Q2;
            {var subQ0=sQuery(id+"F5.wireOp",EDGE,"E100");var subQ1=sQuery(id+"F5.wireOp",EDGE,"E94");var subQ2=makeQuery(id+"F5.imprint","INTERSECT",VERTEX,{"derivedFrom":[subQ1,subQ0]});Q2=makeQuery(id+"F5.imprint","IMPRINT",FACE,{"disambiguationData":[TD([[makeQuery(id+"F5.imprint","IMPRINT",EDGE,{"disambiguationData":[TD([[subQ2,-1.0]])],"derivedFrom":subQ1}),1.0]])]});}
            extrude(context, id + "F7", {"entities" : qUnion([Q0, Q1, Q2]), "depth" : 25 * mm, "offsetDistance" : 25 * mm});
        }
        {
            var Q0;
            Q0=makeQuery(id+"F7.opExtrude","SWEPT_BODY",BODY,{"disambiguationData":[OSD([sQuery(id+"F5.wireOp",EDGE,"E94"),sQuery(id+"F5.wireOp",EDGE,"E100"),sQuery(id+"F5.wireOp",EDGE,"E102")])]});
            deleteBodies(context, id + "F8", {"entities" : qUnion([Q0])});
        }
        {
            var Q0;
            {var subQ5=sQuery(id+"F5.wireOp",EDGE,"E116");Q0=makeQuery(id+"F5.imprint","IMPRINT",FACE,{"disambiguationData":[TD([[makeQuery(id+"F5.imprint","IMPRINT",EDGE,{"derivedFrom":subQ5}),1.0]])]});}
            var Q1;
            {var subQ0=sQuery(id+"F5.wireOp",EDGE,"E109");var subQ3=sQuery(id+"F5.wireOp",EDGE,"E88");var subQ4=makeQuery(id+"F5.imprint","INTERSECT",VERTEX,{"derivedFrom":[subQ3,subQ0]});Q1=makeQuery(id+"F5.imprint","IMPRINT",FACE,{"disambiguationData":[TD([[makeQuery(id+"F5.imprint","IMPRINT",EDGE,{"disambiguationData":[TD([[subQ4,-1.0]])],"derivedFrom":subQ3}),1.0]])]});}
            var Q2;
            {var subQ0=sQuery(id+"F5.wireOp",EDGE,"E101");var subQ1=sQuery(id+"F5.wireOp",EDGE,"E95");var subQ2=makeQuery(id+"F5.imprint","INTERSECT",VERTEX,{"derivedFrom":[subQ1,subQ0]});Q2=makeQuery(id+"F5.imprint","IMPRINT",FACE,{"disambiguationData":[TD([[makeQuery(id+"F5.imprint","IMPRINT",EDGE,{"disambiguationData":[TD([[subQ2,1.0]])],"derivedFrom":subQ1}),1.0]])]});}
            var Q3;
            Q3=makeQuery(id+"F5.imprint","IMPRINT",FACE,{"disambiguationData":[TD([[makeQuery(id+"F5.imprint","IMPRINT",EDGE,{"derivedFrom":sQuery(id+"F5.wireOp",EDGE,"E86")}),-1.0]])]});
            var Q4;
            {var subQ0=sQuery(id+"F5.wireOp",EDGE,"E100");var subQ1=sQuery(id+"F5.wireOp",EDGE,"E94");var subQ2=makeQuery(id+"F5.imprint","INTERSECT",VERTEX,{"derivedFrom":[subQ1,subQ0]});Q4=makeQuery(id+"F5.imprint","IMPRINT",FACE,{"disambiguationData":[TD([[makeQuery(id+"F5.imprint","IMPRINT",EDGE,{"disambiguationData":[TD([[subQ2,-1.0]])],"derivedFrom":subQ1}),1.0]])]});}
            var Q5;
            Q5=makeQuery(id+"F5.imprint","IMPRINT",FACE,{"disambiguationData":[TD([[makeQuery(id+"F5.imprint","IMPRINT",EDGE,{"derivedFrom":sQuery(id+"F5.wireOp",EDGE,"E90.1.0")}),1.0]])]});
            var Q6;
            Q6=makeQuery(id+"F5.imprint","IMPRINT",FACE,{"disambiguationData":[TD([[makeQuery(id+"F5.imprint","IMPRINT",EDGE,{"derivedFrom":sQuery(id+"F5.wireOp",EDGE,"E90.2.0")}),1.0]])]});
            var Q7;
            Q7=makeQuery(id+"F5.imprint","IMPRINT",FACE,{"disambiguationData":[TD([[makeQuery(id+"F5.imprint","IMPRINT",EDGE,{"derivedFrom":sQuery(id+"F5.wireOp",EDGE,"E90.3.0")}),1.0]])]});
            var Q8;
            Q8=makeQuery(id+"F5.imprint","IMPRINT",FACE,{"disambiguationData":[TD([[makeQuery(id+"F5.imprint","IMPRINT",EDGE,{"derivedFrom":sQuery(id+"F5.wireOp",EDGE,"E90.4.0")}),1.0]])]});
            extrude(context, id + "F9", {"entities" : qUnion([Q0, Q1, Q2, Q3, Q4, Q5, Q6, Q7, Q8]), "depth" : 17.5 * mm, "offsetDistance" : 25 * mm});
        }
        {
            var Q0;
            Q0=makeQuery(id+"F7.opExtrude","SWEPT_BODY",BODY,{"disambiguationData":[OSD([sQuery(id+"F5.wireOp",EDGE,"E88"),sQuery(id+"F5.wireOp",EDGE,"E95"),sQuery(id+"F5.wireOp",EDGE,"E101"),sQuery(id+"F5.wireOp",EDGE,"E102"),sQuery(id+"F5.wireOp",EDGE,"E109"),sQuery(id+"F5.wireOp",EDGE,"E110")])]});
            deleteBodies(context, id + "F10", {"entities" : qUnion([Q0])});
        }
        {
            var Q0;
            {var subQ1=sQuery(id+"F5.wireOp",EDGE,"E88");var subQ5=sQuery(id+"F5.wireOp",EDGE,"E109");var subQ8=makeQuery(id+"F5.imprint","INTERSECT",VERTEX,{"derivedFrom":[subQ1,subQ5]});Q0=makeQuery(id+"F5.imprint","IMPRINT",FACE,{"disambiguationData":[TD([[makeQuery(id+"F5.imprint","IMPRINT",EDGE,{"disambiguationData":[TD([[subQ8,1.0]])],"derivedFrom":subQ1}),1.0]])]});}
            var Q1;
            {var subQ0=sQuery(id+"F5.wireOp",EDGE,"E109");var subQ3=sQuery(id+"F5.wireOp",EDGE,"E88");var subQ4=makeQuery(id+"F5.imprint","INTERSECT",VERTEX,{"derivedFrom":[subQ3,subQ0]});Q1=makeQuery(id+"F5.imprint","IMPRINT",FACE,{"disambiguationData":[TD([[makeQuery(id+"F5.imprint","IMPRINT",EDGE,{"disambiguationData":[TD([[subQ4,-1.0]])],"derivedFrom":subQ3}),1.0]])]});}
            var Q2;
            {var subQ0=sQuery(id+"F5.wireOp",EDGE,"E101");var subQ1=sQuery(id+"F5.wireOp",EDGE,"E95");var subQ2=makeQuery(id+"F5.imprint","INTERSECT",VERTEX,{"derivedFrom":[subQ1,subQ0]});Q2=makeQuery(id+"F5.imprint","IMPRINT",FACE,{"disambiguationData":[TD([[makeQuery(id+"F5.imprint","IMPRINT",EDGE,{"disambiguationData":[TD([[subQ2,1.0]])],"derivedFrom":subQ1}),1.0]])]});}
            var Q3;
            {var subQ0=sQuery(id+"F5.wireOp",EDGE,"E100");var subQ1=sQuery(id+"F5.wireOp",EDGE,"E94");var subQ2=makeQuery(id+"F5.imprint","INTERSECT",VERTEX,{"derivedFrom":[subQ1,subQ0]});Q3=makeQuery(id+"F5.imprint","IMPRINT",FACE,{"disambiguationData":[TD([[makeQuery(id+"F5.imprint","IMPRINT",EDGE,{"disambiguationData":[TD([[subQ2,-1.0]])],"derivedFrom":subQ1}),1.0]])]});}
            var Q4;
            {var subQ0=sQuery(id+"F5.wireOp",EDGE,"E115");var subQ1=sQuery(id+"F5.wireOp",EDGE,"E102");var subQ2=makeQuery(id+"F5.imprint","INTERSECT",VERTEX,{"derivedFrom":[subQ1,subQ0]});Q4=makeQuery(id+"F5.imprint","IMPRINT",FACE,{"disambiguationData":[TD([[makeQuery(id+"F5.imprint","IMPRINT",EDGE,{"disambiguationData":[TD([[subQ2,-1.0]])],"derivedFrom":subQ1}),-1.0]])]});}
            var Q5;
            {var subQ0=sQuery(id+"F5.wireOp",EDGE,"E114");var subQ1=sQuery(id+"F5.wireOp",EDGE,"E102");var subQ2=makeQuery(id+"F5.imprint","INTERSECT",VERTEX,{"derivedFrom":[subQ1,subQ0]});Q5=makeQuery(id+"F5.imprint","IMPRINT",FACE,{"disambiguationData":[TD([[makeQuery(id+"F5.imprint","IMPRINT",EDGE,{"disambiguationData":[TD([[subQ2,-1.0]])],"derivedFrom":subQ1}),-1.0]])]});}
            extrude(context, id + "F11", {"entities" : qUnion([Q0, Q1, Q2, Q3, Q4, Q5]), "depth" : 32 * mm, "offsetDistance" : 25 * mm});
        }
        {
            var Q0;
            Q0=qCreatedBy(makeId("Front.planeOp"),FACE);
            var sketch = newSketch(context, id + "F12", { "sketchPlane" : qUnion([Q0])});
            skCircle(sketch, "E233", {"center": v(675.64, -458.14) * mm, "radius": 141 * mm});
            skCircle(sketch, "E234.0", {"center": v(675.64, -458.14) * mm, "radius": 91 * mm});
            skCircle(sketch, "E235", {"center": v(1171.04, -485.62) * mm, "radius": 160 * mm});
            skCircle(sketch, "E236.0", {"center": v(1171.04, -485.62) * mm, "radius": 100 * mm});
            skSolve(sketch);
        }
        {
            var Q0;
            Q0=makeQuery(id+"F12.imprint","IMPRINT",FACE,{"disambiguationData":[TD([[makeQuery(id+"F12.imprint","IMPRINT",EDGE,{"derivedFrom":sQuery(id+"F12.wireOp",EDGE,"E233")}),1.0]])]});
            extrude(context, id + "F13", {"entities" : qUnion([Q0]), "depth" : 25 * mm, "offsetDistance" : 25 * mm});
        }
        {
            var Q0;
            Q0=makeQuery(id+"F12.imprint","IMPRINT",FACE,{"disambiguationData":[TD([[makeQuery(id+"F12.imprint","IMPRINT",EDGE,{"derivedFrom":sQuery(id+"F12.wireOp",EDGE,"E235")}),1.0]])]});
            extrude(context, id + "F14", {"entities" : qUnion([Q0]), "depth" : 25 * mm, "offsetDistance" : 25 * mm});
        }
        {
            var Q0;
            Q0=qCreatedBy(makeId("Front.planeOp"),FACE);
            var sketch = newSketch(context, id + "F15", { "sketchPlane" : qUnion([Q0])});
            skArc(sketch, "E237", {"start": v(1792.56, -500) * mm, "mid": v(1741.5, -515.68) * mm, "end": v(1698.51, -547.39) * mm});
            skArc(sketch, "E238.0", {"start": v(1794.28, -558.43) * mm, "mid": v(1767.6, -567.47) * mm, "end": v(1744.46, -583.53) * mm});
            skLineSegment(sketch, "E239.trimOffspring", {"start": v(1730.97, -583.62) * mm, "end": v(1698.77, -554.57) * mm});
            skLineSegment(sketch, "E240.trimOffspring", {"start": v(1802.37, -547.64) * mm, "end": v(1798.18, -504.47) * mm});
            skArc(sketch, "E241.filletArc", {"start": v(1698.51, -547.39) * mm, "mid": v(1697.12, -551.03) * mm, "end": v(1698.77, -554.57) * mm});
            skArc(sketch, "E242.filletArc", {"start": v(1798.18, -504.47) * mm, "mid": v(1796.32, -501.04) * mm, "end": v(1792.56, -500) * mm});
            skArc(sketch, "E243.filletArc", {"start": v(1730.97, -583.62) * mm, "mid": v(1737.73, -586.2) * mm, "end": v(1744.46, -583.53) * mm});
            skArc(sketch, "E244.filletArc", {"start": v(1794.28, -558.43) * mm, "mid": v(1800.42, -554.6) * mm, "end": v(1802.37, -547.64) * mm});
            skArc(sketch, "E245", {"start": v(2300.52, -624.52) * mm, "mid": v(2291.28, -571.45) * mm, "end": v(2262.7, -525.79) * mm});
            skArc(sketch, "E246.0", {"start": v(2252.21, -629.38) * mm, "mid": v(2246.46, -588.62) * mm, "end": v(2223.5, -554.44) * mm});
            skLineSegment(sketch, "E247", {"start": v(2160.55, -621.53) * mm, "end": v(2338.52, -553.35) * mm});
            skLineSegment(sketch, "E248", {"start": v(2224.52, -543.44) * mm, "end": v(2253.8, -524.68) * mm});
            skLineSegment(sketch, "E249", {"start": v(2260.32, -636.89) * mm, "end": v(2294.65, -631.28) * mm});
            skPoint(sketch, "E250.visualSharp", {"position": v(2216.56, -548.54) * mm});
            skArc(sketch, "E250.filletArc", {"start": v(2224.52, -543.44) * mm, "mid": v(2221.33, -548.7) * mm, "end": v(2223.5, -554.44) * mm});
            skPoint(sketch, "E251.visualSharp", {"position": v(2250.99, -638.41) * mm});
            skArc(sketch, "E251.filletArc", {"start": v(2252.21, -629.38) * mm, "mid": v(2254.43, -635.11) * mm, "end": v(2260.32, -636.89) * mm});
            skPoint(sketch, "E252.visualSharp", {"position": v(2258.6, -521.6) * mm});
            skArc(sketch, "E252.filletArc", {"start": v(2262.7, -525.79) * mm, "mid": v(2258.45, -523.63) * mm, "end": v(2253.8, -524.68) * mm});
            skPoint(sketch, "E253.visualSharp", {"position": v(2300.27, -630.36) * mm});
            skArc(sketch, "E253.filletArc", {"start": v(2294.65, -631.28) * mm, "mid": v(2298.8, -628.96) * mm, "end": v(2300.52, -624.52) * mm});
            skSolve(sketch);
        }
        {
            var Q0;
            Q0=makeQuery(id+"F15.imprint","IMPRINT",FACE,{"disambiguationData":[TD([[makeQuery(id+"F15.imprint","IMPRINT",EDGE,{"derivedFrom":sQuery(id+"F15.wireOp",EDGE,"E237")}),1.0]])]});
            extrude(context, id + "F16", {"entities" : qUnion([Q0]), "depth" : 10 * mm, "offsetDistance" : 25 * mm});
        }
        {
            var Q0;
            Q0=makeQuery(id+"F15.imprint","IMPRINT",FACE,{"disambiguationData":[TD([[makeQuery(id+"F15.imprint","IMPRINT",EDGE,{"derivedFrom":sQuery(id+"F15.wireOp",EDGE,"E248")}),-1.0]])]});
            var Q1;
            Q1=makeQuery(id+"F15.imprint","IMPRINT",FACE,{"disambiguationData":[TD([[makeQuery(id+"F15.imprint","IMPRINT",EDGE,{"derivedFrom":sQuery(id+"F15.wireOp",EDGE,"E249")}),1.0]])]});
            extrude(context, id + "F17", {"entities" : qUnion([Q0, Q1]), "depth" : 10 * mm, "offsetDistance" : 25 * mm});
        }
        {
            var Q0;
            Q0=makeQuery(id+"F5.imprint","IMPRINT",FACE,{"disambiguationData":[TD([[makeQuery(id+"F5.imprint","IMPRINT",EDGE,{"derivedFrom":sQuery(id+"F5.wireOp",EDGE,"E173.0")}),-1.0]])]});
            var Q1;
            Q1=makeQuery(id+"F5.imprint","IMPRINT",FACE,{"disambiguationData":[TD([[makeQuery(id+"F5.imprint","IMPRINT",EDGE,{"derivedFrom":sQuery(id+"F5.wireOp",EDGE,"E184")}),-1.0]])]});
            extrude(context, id + "F18", {"entities" : qUnion([Q0, Q1]), "depth" : 12 * mm, "offsetDistance" : 25 * mm});
        }
        {
            var Q0;
            Q0=makeQuery(id+"F5.imprint","IMPRINT",FACE,{"disambiguationData":[TD([[makeQuery(id+"F5.imprint","IMPRINT",EDGE,{"derivedFrom":sQuery(id+"F5.wireOp",EDGE,"E181")}),-1.0]])]});
            var Q1;
            Q1=makeQuery(id+"F5.imprint","IMPRINT",FACE,{"disambiguationData":[TD([[makeQuery(id+"F5.imprint","IMPRINT",EDGE,{"derivedFrom":sQuery(id+"F5.wireOp",EDGE,"E183")}),-1.0]])]});
            extrude(context, id + "F19", {"entities" : qUnion([Q0, Q1]), "operationType" : NewBodyOperationType.ADD, "depth" : 28 * mm, "offsetDistance" : 25 * mm});
        }
    });
